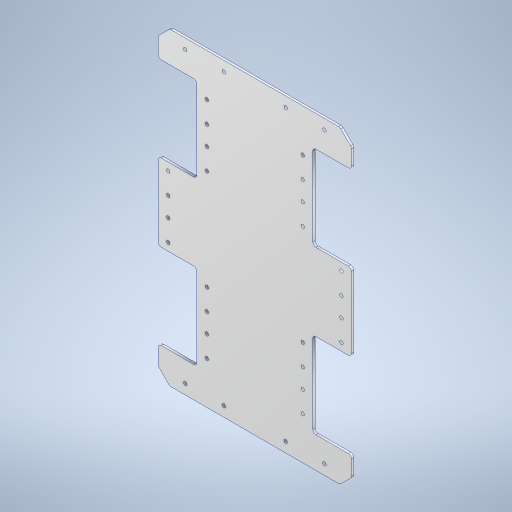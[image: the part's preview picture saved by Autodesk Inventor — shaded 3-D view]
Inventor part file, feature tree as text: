
AUTODESK INVENTOR PART (.ipt)
format: ipt  version: 2024 (Build 280153000, 153)  size: 435,200 bytes
history: native  units: mm
features: extrude x4, sketch x4, fillet x1
ambient origin geometry x8: Origin, YZ Plane, XZ Plane, XY Plane, X Axis, Y Axis, Z Axis, Center Point
bodies: Volumenkörper1 (feature_tree)
feature tree (9):
  extrude  "Extrusion1"  Depth=250.0mm
  extrude  "Extrusion7"  Depth=3.0mm
  sketch  "Skizze6"  dims[d2=3.0mm d3=0.0mm d57=15.0mm]
  extrude  "Extrusion11"  Depth=10.0mm TaperAngle=0.0deg
  extrude  "Extrusion12"  Depth=40.0mm
  fillet  "Rundung1"  Radius=50.0mm
  sketch  "Skizze1"  dims[d0=400.0mm d1=250.0mm]
  sketch  "Skizze7"  dims[d58=15.0mm d59=10.0mm d60=0.0mm]
  sketch  "Skizze9"  dims[d74=110.0mm d75=40.0mm d76=50.0mm d77=110.0mm d78=50.0mm d79=110.0mm d80=50.0mm d83=10.0mm d84=0.0mm d85=13.0mm d86=4.5mm d87=4.5mm d88=4.5mm d89=4.5mm d90=25.0mm d91=80.0mm d92=13.0mm d93=4.5mm d94=4.5mm d95=4.5mm d96=4.5mm d97=25.0mm d98=80.0mm d99=13.0mm d100=4.5mm d101=4.5mm d102=4.5mm d103=4.5mm d104=80.0mm d105=180.0mm d106=10.0mm d107=0.0mm d108=4.0mm d34=0.5mm d35=0.872665mm d36=0.5mm d37=0.872665mm]
